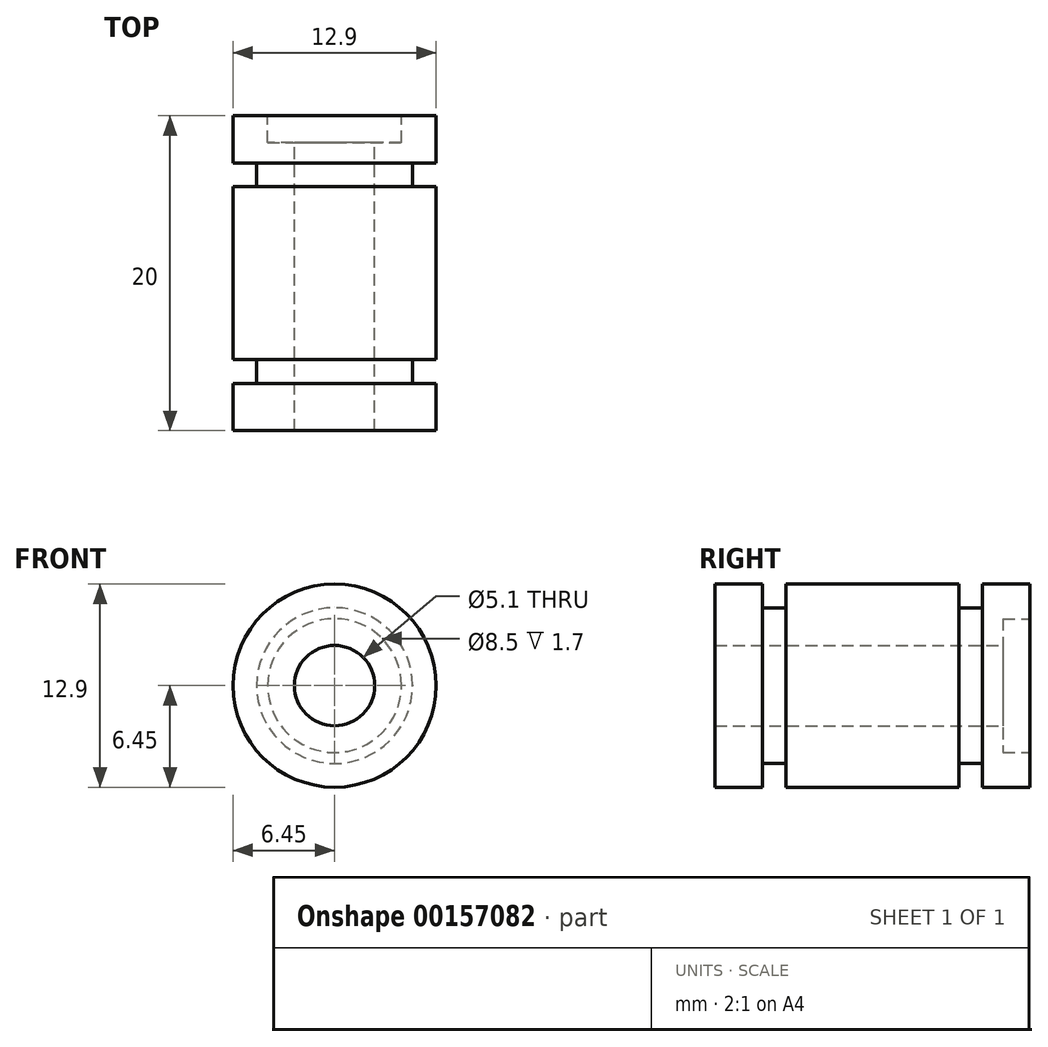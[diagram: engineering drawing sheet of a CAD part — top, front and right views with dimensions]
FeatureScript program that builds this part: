
annotation { "Feature Type Name" : "Feature", "Feature Type Description" : "" }
export const myFeature = defineFeature(function(context is Context, id is Id, definition is map)
    precondition{}
    {
        {
            var Q0;
            Q0=qCreatedBy(makeId("Right.planeOp"),FACE);
            var sketch = newSketch(context, id + "F0", { "sketchPlane" : qUnion([Q0])});
            skLineSegment(sketch, "E0", {"start": v(11.47, 0) * mm, "end": v(0, 0) * mm, "construction": true});
            skLineSegment(sketch, "E1", {"start": v(18.3, 2.55) * mm, "end": v(0, 2.55) * mm});
            skLineSegment(sketch, "E2", {"start": v(18.3, 2.55) * mm, "end": v(18.3, 4.25) * mm});
            skLineSegment(sketch, "E3", {"start": v(20, 4.25) * mm, "end": v(18.3, 4.25) * mm});
            skLineSegment(sketch, "E4", {"start": v(20, 4.25) * mm, "end": v(20, 6.45) * mm});
            skLineSegment(sketch, "E5", {"start": v(17, 6.45) * mm, "end": v(20, 6.45) * mm});
            skLineSegment(sketch, "E6", {"start": v(17, 6.45) * mm, "end": v(17, 4.95) * mm});
            skLineSegment(sketch, "E7", {"start": v(15.5, 4.95) * mm, "end": v(17, 4.95) * mm});
            skLineSegment(sketch, "E8", {"start": v(3, 4.95) * mm, "end": v(3, 6.45) * mm});
            skLineSegment(sketch, "E9", {"start": v(0, 6.45) * mm, "end": v(3, 6.45) * mm});
            skLineSegment(sketch, "E10", {"start": v(0, 6.45) * mm, "end": v(0, 2.55) * mm});
            skLineSegment(sketch, "E11", {"start": v(4.5, 4.95) * mm, "end": v(4.5, 6.45) * mm});
            skLineSegment(sketch, "E12", {"start": v(4.5, 6.45) * mm, "end": v(15.5, 6.45) * mm});
            skLineSegment(sketch, "E13", {"start": v(15.5, 6.45) * mm, "end": v(15.5, 4.95) * mm});
            skLineSegment(sketch, "E14.trimOffspring", {"start": v(4.5, 4.95) * mm, "end": v(3, 4.95) * mm});
            skSolve(sketch);
        }
        {
            var Q0;
            Q0=makeQuery(id+"F0.imprint","IMPRINT",FACE,{"disambiguationData":[TD([[makeQuery(id+"F0.imprint","IMPRINT",EDGE,{"derivedFrom":sQuery(id+"F0.wireOp",EDGE,"E1")}),-1.0]])]});
            var Q1;
            Q1=sQuery(id+"F0.wireOp",EDGE,"E0");
            revolve(context, id + "F1", {"entities" : qUnion([Q0]), "axis" : qUnion([Q1]), "revolveType" : RevolveType.FULL});
        }
    });
